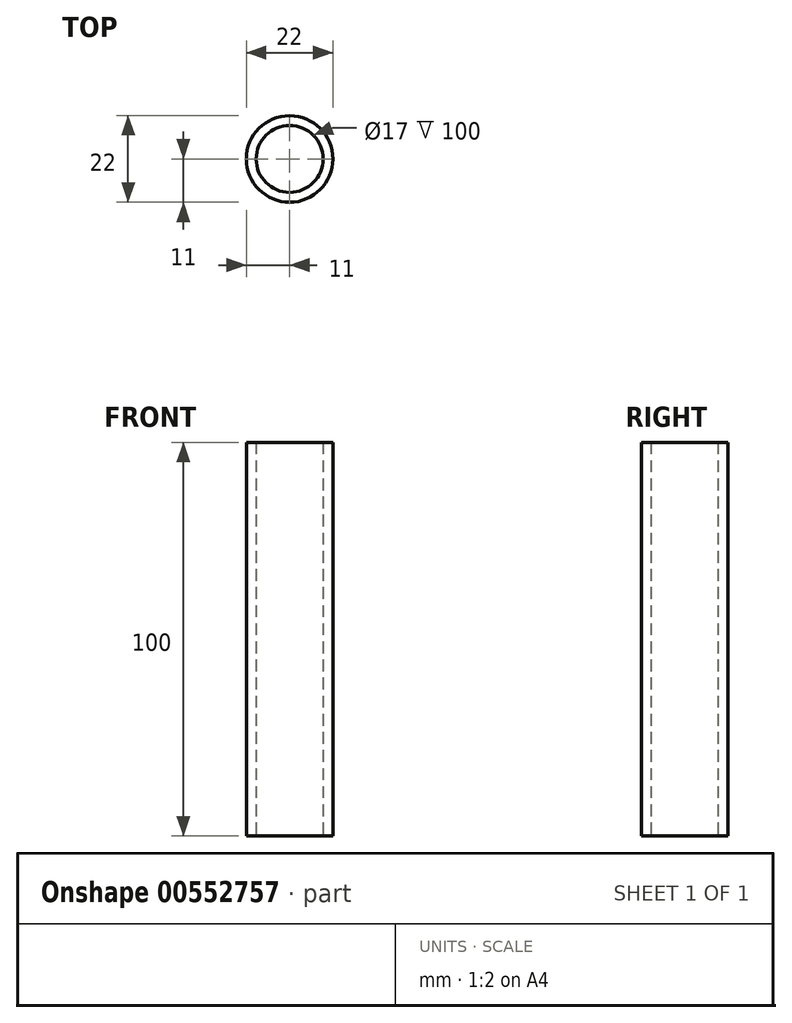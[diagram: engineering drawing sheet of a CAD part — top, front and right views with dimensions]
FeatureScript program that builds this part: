
annotation { "Feature Type Name" : "Feature", "Feature Type Description" : "" }
export const myFeature = defineFeature(function(context is Context, id is Id, definition is map)
    precondition{}
    {
        {
            var Q0;
            Q0=qCreatedBy(makeId("Top.planeOp"),FACE);
            var sketch = newSketch(context, id + "F0", { "sketchPlane" : qUnion([Q0])});
            skCircle(sketch, "E0", {"center": v(0, 0) * mm, "radius": 8.5 * mm});
            skCircle(sketch, "E1.0", {"center": v(0, 0) * mm, "radius": 11 * mm});
            skSolve(sketch);
        }
        {
            var Q0;
            Q0 = qSketchRegion(id + "F0", true);
            extrude(context, id + "F1", {"entities" : qUnion([Q0]), "depth" : 100 * mm, "offsetDistance" : 25 * mm});
        }
    });
